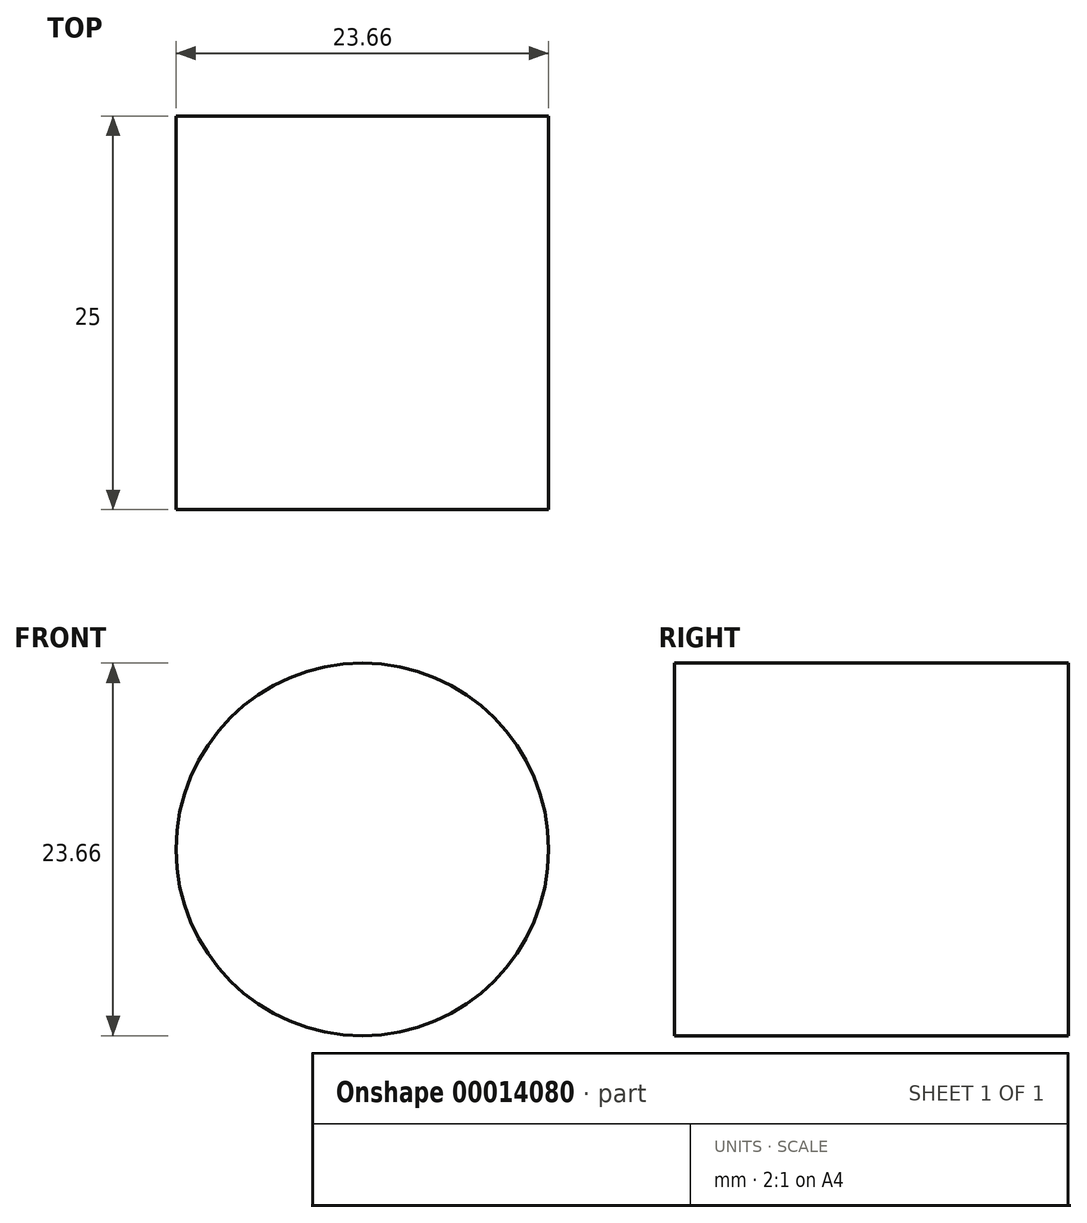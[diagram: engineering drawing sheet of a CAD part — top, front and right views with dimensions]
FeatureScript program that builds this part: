
annotation { "Feature Type Name" : "Feature", "Feature Type Description" : "" }
export const myFeature = defineFeature(function(context is Context, id is Id, definition is map)
    precondition{}
    {
        {
            var Q0;
            Q0=qCreatedBy(makeId("Front.planeOp"),FACE);
            var sketch = newSketch(context, id + "F0", { "sketchPlane" : qUnion([Q0])});
            skLineSegment(sketch, "E0", {"start": v(0, 0) * mm, "end": v(0, 95.84) * mm});
            skCircle(sketch, "E1", {"center": v(0, 0) * mm, "radius": 11.83 * mm});
            skSolve(sketch);
        }
        {
            var Q0;
            Q0 = qSketchRegion(id + "F0", true);
            extrude(context, id + "F1", {"entities" : qUnion([Q0]), "depth" : 25 * mm});
        }
    });
